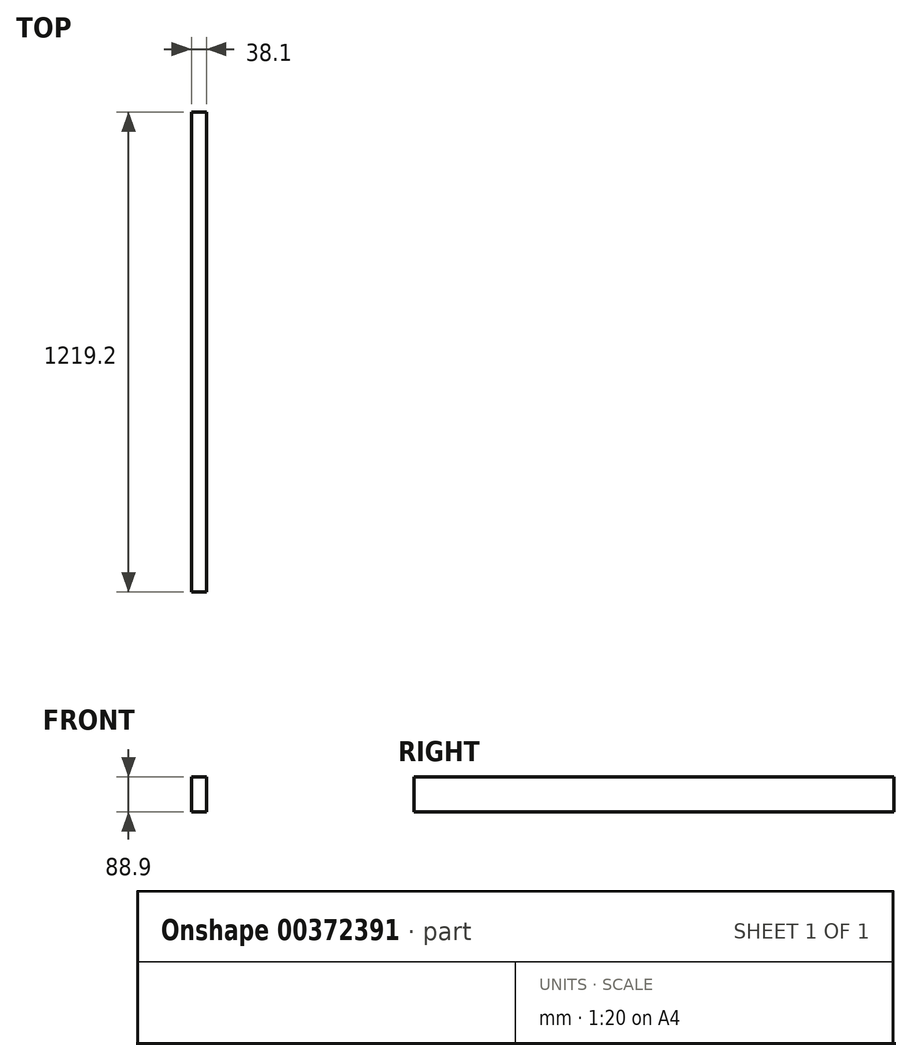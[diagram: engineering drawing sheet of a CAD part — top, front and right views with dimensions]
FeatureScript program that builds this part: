
annotation { "Feature Type Name" : "Feature", "Feature Type Description" : "" }
export const myFeature = defineFeature(function(context is Context, id is Id, definition is map)
    precondition{}
    {
        {
            var Q0;
            Q0=qCreatedBy(makeId("Front.planeOp"),FACE);
            var sketch = newSketch(context, id + "F0", { "sketchPlane" : qUnion([Q0])});
            skLineSegment(sketch, "E0.bottom", {"start": v(-19.05, 44.45) * mm, "end": v(19.05, 44.45) * mm});
            skLineSegment(sketch, "E0.top", {"start": v(-19.05, -44.45) * mm, "end": v(19.05, -44.45) * mm});
            skLineSegment(sketch, "E0.left", {"start": v(-19.05, 44.45) * mm, "end": v(-19.05, -44.45) * mm});
            skLineSegment(sketch, "E0.right", {"start": v(19.05, 44.45) * mm, "end": v(19.05, -44.45) * mm});
            skPoint(sketch, "E0.middle", {"position": v(0, 0) * mm});
            skSolve(sketch);
        }
        {
            var Q0;
            Q0=qSketchRegion(id+"F0",true);
            extrude(context, id + "F1", {"entities" : qUnion([Q0]), "endBound" : BoundingType.SYMMETRIC, "oppositeDirection" : true, "depth" : 1219.2 * mm});
        }
    });
